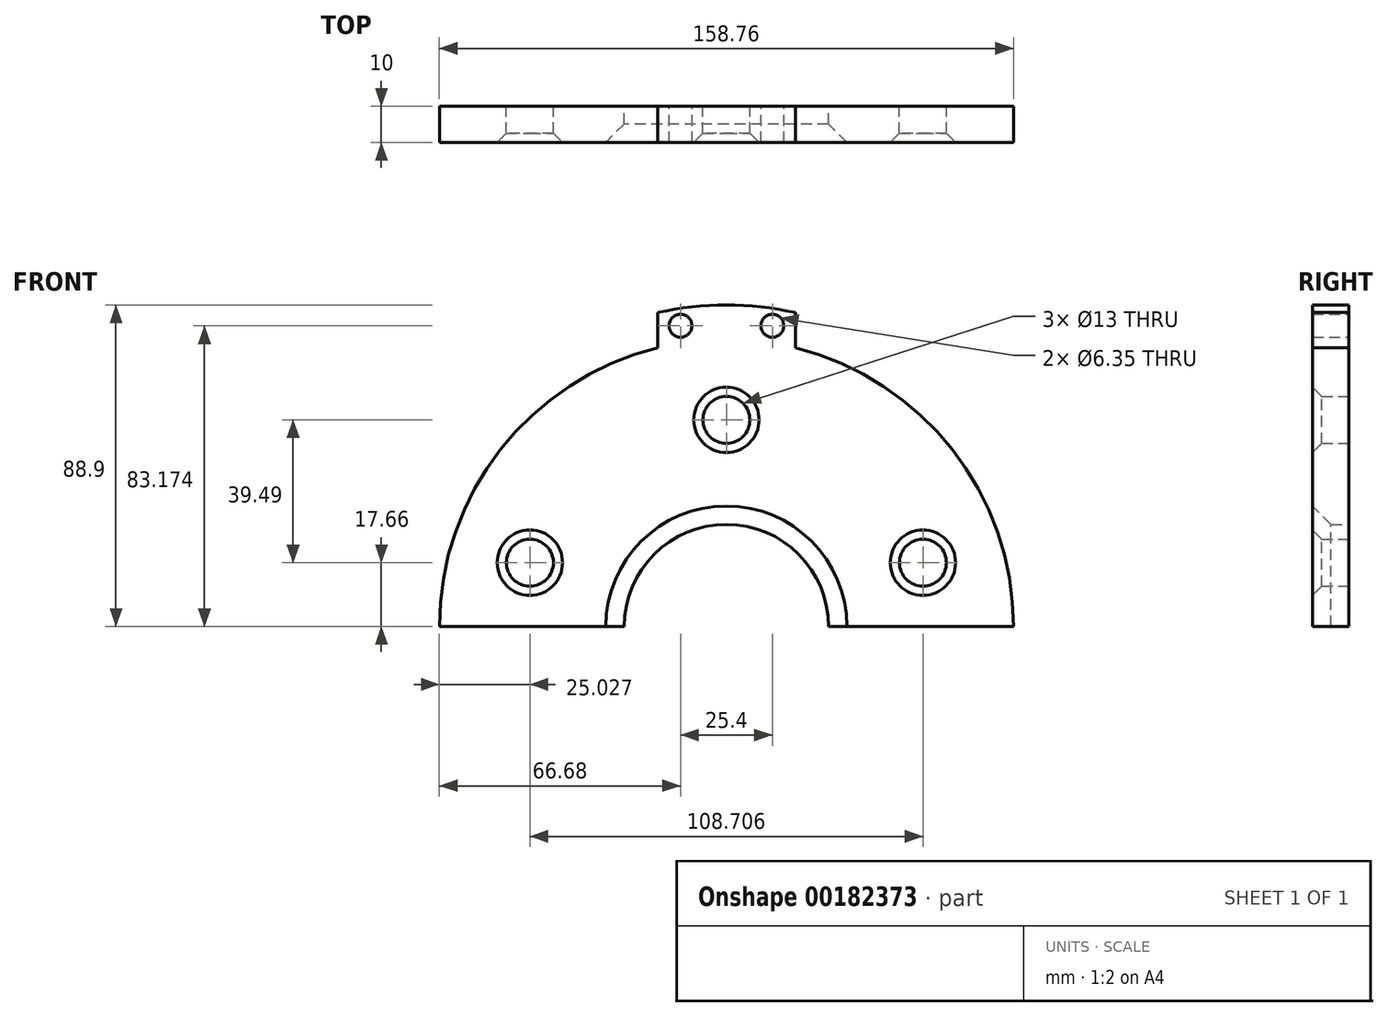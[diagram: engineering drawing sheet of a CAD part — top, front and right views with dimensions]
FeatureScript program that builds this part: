
annotation { "Feature Type Name" : "Feature", "Feature Type Description" : "" }
export const myFeature = defineFeature(function(context is Context, id is Id, definition is map)
    precondition{}
    {
        {
            var Q0;
            Q0=qCreatedBy(makeId("Front.planeOp"),FACE);
            var sketch = newSketch(context, id + "F2", { "sketchPlane" : qUnion([Q0])});
            skArc(sketch, "E0", {"start": v(-19.05, 77.06) * mm, "mid": v(-62.5, 48.93) * mm, "end": v(-79.37, 0) * mm});
            skCircle(sketch, "E1", {"center": v(0, 57.15) * mm, "radius": 6.5 * mm});
            skCircle(sketch, "E2.1.0", {"center": v(-54.35, 17.66) * mm, "radius": 6.5 * mm});
            skCircle(sketch, "E2.4.0", {"center": v(54.35, 17.66) * mm, "radius": 6.5 * mm});
            skArc(sketch, "E3", {"start": v(28.25, 0) * mm, "mid": v(0, 28.25) * mm, "end": v(-28.25, 0) * mm});
            skArc(sketch, "E4", {"start": v(57.15, 0) * mm, "mid": v(-52.31, 23) * mm, "end": v(38.62, -42.12) * mm, "construction": true});
            skArc(sketch, "E5", {"start": v(19.05, 86.83) * mm, "mid": v(0, 88.9) * mm, "end": v(-19.05, 86.83) * mm});
            skLineSegment(sketch, "E6", {"start": v(-19.05, 86.83) * mm, "end": v(-19.05, 77.06) * mm});
            skLineSegment(sketch, "E7", {"start": v(0, 0) * mm, "end": v(0, 79.38) * mm, "construction": true});
            skLineSegment(sketch, "E8.MirrorCS", {"start": v(19.05, 86.83) * mm, "end": v(19.05, 77.06) * mm});
            skCircle(sketch, "E9", {"center": v(0, 0) * mm, "radius": 84.14 * mm, "construction": true});
            skCircle(sketch, "E10", {"center": v(-12.7, 83.17) * mm, "radius": 3.18 * mm});
            skCircle(sketch, "E11.MirrorC", {"center": v(12.7, 83.17) * mm, "radius": 3.18 * mm});
            skLineSegment(sketch, "E12", {"start": v(-79.38, 0) * mm, "end": v(-28.25, 0) * mm});
            skLineSegment(sketch, "E13.trimOffspring", {"start": v(28.25, 0) * mm, "end": v(79.38, 0) * mm});
            skArc(sketch, "E14.trimOffspring", {"start": v(79.37, 0) * mm, "mid": v(62.5, 48.93) * mm, "end": v(19.05, 77.06) * mm});
            skSolve(sketch);
        }
        {
            var Q0;
            Q0 = qSketchRegion(id + "F2", true);
            extrude(context, id + "F3", {"entities" : qUnion([Q0]), "depth" : 10 * mm});
        }
        {
            var Q0;
            Q0=makeQuery(id+"F3.opExtrude","CAP_EDGE",EDGE,{"disambiguationData":[OSD([sQuery(id+"F2.wireOp",EDGE,"E3")])],"isStart":false});
            chamfer(context, id + "F0", {"entities" : qUnion([Q0]), "width" : 5.08 * mm, "tangentPropagation" : true});
        }
        {
            var Q0;
            Q0=makeQuery(id+"F3.opExtrude","CAP_EDGE",EDGE,{"disambiguationData":[OSD([sQuery(id+"F2.wireOp",EDGE,"E1")])],"isStart":false});
            var Q1;
            Q1=makeQuery(id+"F3.opExtrude","CAP_EDGE",EDGE,{"disambiguationData":[OSD([sQuery(id+"F2.wireOp",EDGE,"E2.1.0")])],"isStart":false});
            var Q2;
            Q2=makeQuery(id+"F3.opExtrude","CAP_EDGE",EDGE,{"disambiguationData":[OSD([sQuery(id+"F2.wireOp",EDGE,"E2.4.0")])],"isStart":false});
            var Q3;
            Q3=makeQuery(id+"F3.opExtrude","CAP_EDGE",EDGE,{"disambiguationData":[OSD([sQuery(id+"F2.wireOp",EDGE,"E2.2.0")])],"isStart":false});
            var Q4;
            Q4=makeQuery(id+"F3.opExtrude","CAP_EDGE",EDGE,{"disambiguationData":[OSD([sQuery(id+"F2.wireOp",EDGE,"E2.3.0")])],"isStart":false});
            chamfer(context, id + "F1", {"entities" : qUnion([Q0, Q1, Q2, Q3, Q4]), "width" : 2.54 * mm, "tangentPropagation" : true});
        }
    });
